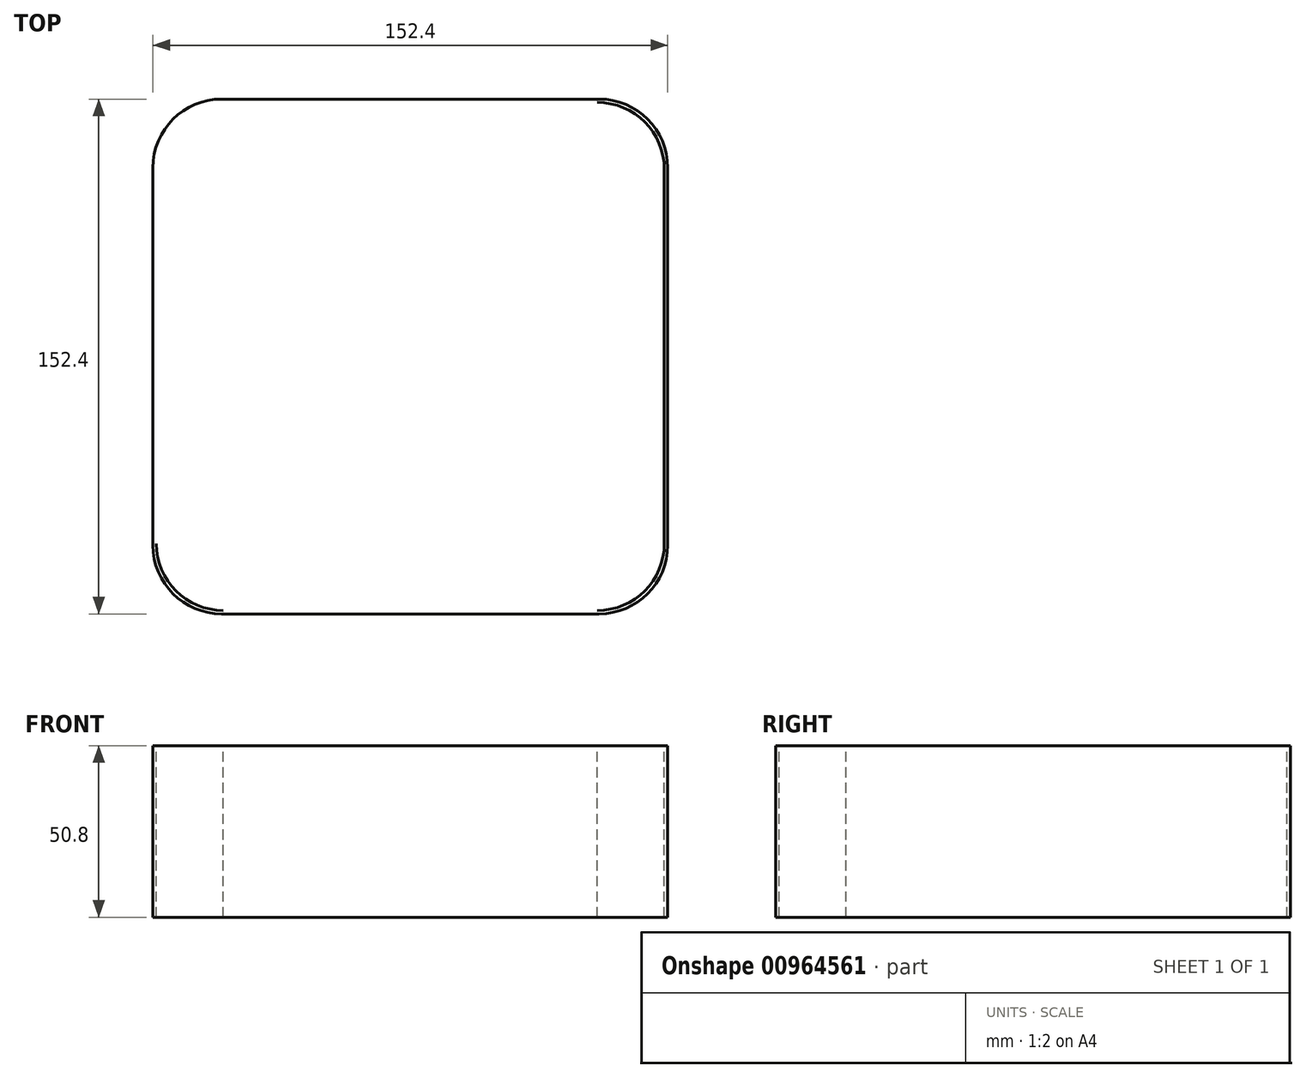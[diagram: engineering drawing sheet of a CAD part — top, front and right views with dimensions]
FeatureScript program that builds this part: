
annotation { "Feature Type Name" : "Feature", "Feature Type Description" : "" }
export const myFeature = defineFeature(function(context is Context, id is Id, definition is map)
    precondition{}
    {
        {
            var Q0;
            Q0=qCreatedBy(makeId("Top.planeOp"),FACE);
            var sketch = newSketch(context, id + "F0", { "sketchPlane" : qUnion([Q0])});
            skLineSegment(sketch, "E0.bottom", {"start": v(55.88, -76.2) * mm, "end": v(-55.88, -76.2) * mm});
            skLineSegment(sketch, "E0.top", {"start": v(55.88, 76.2) * mm, "end": v(-55.88, 76.2) * mm});
            skLineSegment(sketch, "E0.left", {"start": v(76.2, -55.88) * mm, "end": v(76.2, 55.88) * mm});
            skLineSegment(sketch, "E0.right", {"start": v(-76.2, -55.88) * mm, "end": v(-76.2, 55.88) * mm});
            skPoint(sketch, "E0.middle", {"position": v(0, 0) * mm});
            skPoint(sketch, "E1.visualSharp", {"position": v(-76.2, 76.2) * mm});
            skArc(sketch, "E1.filletArc", {"start": v(-55.88, 76.2) * mm, "mid": v(-70.25, 70.25) * mm, "end": v(-76.2, 55.88) * mm});
            skPoint(sketch, "E2.visualSharp", {"position": v(76.2, 76.2) * mm});
            skArc(sketch, "E2.filletArc", {"start": v(76.2, 55.88) * mm, "mid": v(70.25, 70.25) * mm, "end": v(55.88, 76.2) * mm});
            skLineSegment(sketch, "E3.bottom", {"start": v(55.39, 75.2) * mm, "end": v(-55.39, 75.2) * mm});
            skLineSegment(sketch, "E3.top", {"start": v(55.39, -75.2) * mm, "end": v(-55.39, -75.2) * mm});
            skLineSegment(sketch, "E3.left", {"start": v(75.2, 55.38) * mm, "end": v(75.2, -55.38) * mm});
            skLineSegment(sketch, "E3.right", {"start": v(-75.2, 55.38) * mm, "end": v(-75.2, -55.38) * mm});
            skPoint(sketch, "E4.visualSharp", {"position": v(75.2, 75.2) * mm});
            skArc(sketch, "E4.filletArc", {"start": v(75.2, 55.38) * mm, "mid": v(69.4, 69.4) * mm, "end": v(55.39, 75.2) * mm});
            skPoint(sketch, "E5.visualSharp", {"position": v(-75.2, 75.2) * mm});
            skArc(sketch, "E5.filletArc", {"start": v(-55.39, 75.2) * mm, "mid": v(-69.4, 69.4) * mm, "end": v(-75.2, 55.38) * mm});
            skPoint(sketch, "E6.visualSharp", {"position": v(76.2, -76.2) * mm});
            skArc(sketch, "E6.filletArc", {"start": v(55.88, -76.2) * mm, "mid": v(70.25, -70.25) * mm, "end": v(76.2, -55.88) * mm});
            skPoint(sketch, "E7.visualSharp", {"position": v(75.2, -75.2) * mm});
            skArc(sketch, "E7.filletArc", {"start": v(55.39, -75.2) * mm, "mid": v(69.4, -69.4) * mm, "end": v(75.2, -55.38) * mm});
            skPoint(sketch, "E8.visualSharp", {"position": v(-75.2, -75.2) * mm});
            skArc(sketch, "E8.filletArc", {"start": v(-75.2, -55.38) * mm, "mid": v(-69.4, -69.4) * mm, "end": v(-55.39, -75.2) * mm});
            skPoint(sketch, "E9.visualSharp", {"position": v(-76.2, -76.2) * mm});
            skArc(sketch, "E9.filletArc", {"start": v(-76.2, -55.88) * mm, "mid": v(-70.25, -70.25) * mm, "end": v(-55.88, -76.2) * mm});
            skSolve(sketch);
        }
        {
            var Q0;
            Q0=makeQuery(id+"F0.imprint","IMPRINT",FACE,{"disambiguationData":[TD([[makeQuery(id+"F0.imprint","IMPRINT",EDGE,{"derivedFrom":sQuery(id+"F0.wireOp",EDGE,"E0.bottom")}),-1.0]])]});
            var Q1;
            Q1=sQuery(id+"F0.wireOp",EDGE,"E8.filletArc");
            var Q2;
            Q2=sQuery(id+"F0.wireOp",EDGE,"E9.filletArc");
            var Q3;
            Q3=sQuery(id+"F0.wireOp",EDGE,"E0.right");
            var Q4;
            Q4=sQuery(id+"F0.wireOp",EDGE,"E1.filletArc");
            var Q5;
            Q5=sQuery(id+"F0.wireOp",EDGE,"E0.top");
            var Q6;
            Q6=sQuery(id+"F0.wireOp",EDGE,"E2.filletArc");
            var Q7;
            Q7=sQuery(id+"F0.wireOp",EDGE,"E3.left");
            var Q8;
            Q8=sQuery(id+"F0.wireOp",EDGE,"E7.filletArc");
            var Q9;
            Q9=sQuery(id+"F0.wireOp",EDGE,"E4.filletArc");
            var Q10;
            Q10=sQuery(id+"F0.wireOp",EDGE,"E6.filletArc");
            var Q11;
            Q11=sQuery(id+"F0.wireOp",EDGE,"E0.left");
            var Q12;
            Q12=sQuery(id+"F0.wireOp",EDGE,"E0.bottom");
            var Q13;
            Q13=qCreatedBy(makeId("Top.planeOp"),FACE);
            extrude(context, id + "F1", {"entities" : qUnion([Q0]), "bodyType" : ToolBodyType.SURFACE, "surfaceEntities" : qUnion([Q1, Q2, Q3, Q4, Q5, Q6, Q7, Q8, Q9, Q10, Q11, Q12]), "endBound" : BoundingType.SYMMETRIC, "depth" : 50.8 * mm, "endBoundEntityFace" : qUnion([Q13]), "offsetDistance" : 25.4 * mm});
        }
    });
